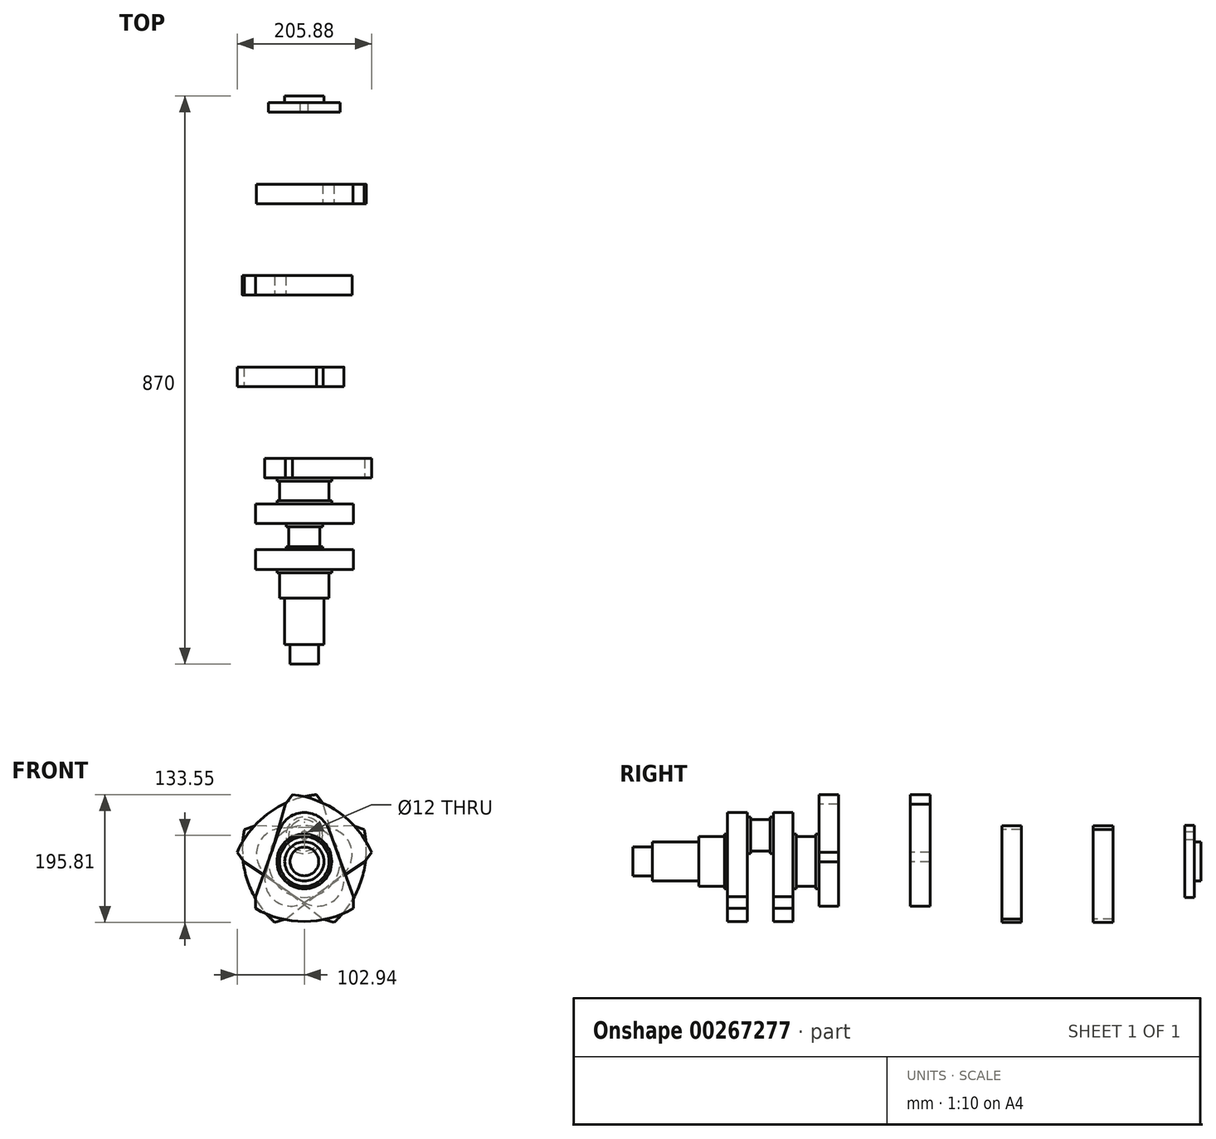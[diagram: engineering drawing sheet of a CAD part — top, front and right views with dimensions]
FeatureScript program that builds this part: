
annotation { "Feature Type Name" : "Feature", "Feature Type Description" : "" }
export const myFeature = defineFeature(function(context is Context, id is Id, definition is map)
    precondition{}
    {
        {
            assignVariable(context, id + "F0", {"name" : "wangen_breite", "anyValue" : 30});
        }
        {
            assignVariable(context, id + "F1", {"name" : "lager_klein_breite", "anyValue" : 40});
        }
        {
            assignVariable(context, id + "F2", {"name" : "lager_gross_breite", "anyValue" : 40});
        }
        {
            assignVariable(context, id + "F3", {"name" : "pleuel_breite", "anyValue" : 2 * getVariable(context, 'wangen_breite') + getVariable(context, 'lager_gross_breite') + getVariable(context, 'lager_klein_breite')});
        }
        {
            var Q0;
            Q0=qCreatedBy(makeId("Front.planeOp"),FACE);
            var sketch = newSketch(context, id + "F4", { "sketchPlane" : qUnion([Q0])});
            skLineSegment(sketch, "E0", {"start": v(-37.59, 48.68) * mm, "end": v(-75, -54.1) * mm});
            skLineSegment(sketch, "E1", {"start": v(-75, -54.1) * mm, "end": v(-75, -71.9) * mm});
            skLineSegment(sketch, "E2", {"start": v(75, -71.9) * mm, "end": v(75, -54.1) * mm});
            skLineSegment(sketch, "E3", {"start": v(75, -54.1) * mm, "end": v(37.59, 48.68) * mm});
            skArc(sketch, "E4", {"start": v(37.59, 48.68) * mm, "mid": v(0, 75) * mm, "end": v(-37.59, 48.68) * mm});
            skArc(sketch, "E5", {"start": v(-75, -71.9) * mm, "mid": v(0, -92) * mm, "end": v(75, -71.9) * mm});
            skSolve(sketch);
        }
        {
            var Q0;
            Q0 = qSketchRegion(id + "F4", true);
            extrude(context, id + "F5", {"entities" : qUnion([Q0]), "oppositeDirection" : true, "depth" : (getVariable(context, 'wangen_breite')) * mm});
        }
        {
            var Q0;
            Q0=qCreatedBy(makeId("Right.planeOp"),FACE);
            var sketch = newSketch(context, id + "F6", { "sketchPlane" : qUnion([Q0])});
            skLineSegment(sketch, "E6", {"start": v(0, 0) * mm, "end": v(0, 28) * mm});
            skLineSegment(sketch, "E7", {"start": v(0, 28) * mm, "end": v(5, 28) * mm});
            skLineSegment(sketch, "E8", {"start": v(5, 28) * mm, "end": v(5, 24) * mm});
            skLineSegment(sketch, "E9", {"start": v(5, 24) * mm, "end": v(35, 24) * mm});
            skLineSegment(sketch, "E10", {"start": v(35, 24) * mm, "end": v(35, 28) * mm});
            skLineSegment(sketch, "E11", {"start": v(35, 28) * mm, "end": v(40, 28) * mm});
            skLineSegment(sketch, "E12", {"start": v(40, 28) * mm, "end": v(40, 0) * mm});
            skLineSegment(sketch, "E13", {"start": v(40, 0) * mm, "end": v(0, 0) * mm});
            skSolve(sketch);
        }
        {
            var Q0;
            Q0 = qSketchRegion(id + "F6", true);
            var Q1;
            Q1=sQuery(id+"F6.wireOp",EDGE,"E13");
            revolve(context, id + "F7", {"entities" : qUnion([Q0]), "axis" : qUnion([Q1]), "revolveType" : RevolveType.FULL});
        }
        {
            var Q0;
            Q0=qCreatedBy(makeId("Right.planeOp"),FACE);
            var sketch = newSketch(context, id + "F8", { "sketchPlane" : qUnion([Q0])});
            skLineSegment(sketch, "E14", {"start": v(0, 0) * mm, "end": v(0, 42) * mm});
            skLineSegment(sketch, "E15", {"start": v(0, 42) * mm, "end": v(5, 42) * mm});
            skLineSegment(sketch, "E16", {"start": v(5, 42) * mm, "end": v(5, 38) * mm});
            skLineSegment(sketch, "E17", {"start": v(5, 38) * mm, "end": v(35, 38) * mm});
            skLineSegment(sketch, "E18", {"start": v(35, 38) * mm, "end": v(35, 42) * mm});
            skLineSegment(sketch, "E19", {"start": v(35, 42) * mm, "end": v(40, 42) * mm});
            skLineSegment(sketch, "E20", {"start": v(40, 42) * mm, "end": v(40, 0) * mm});
            skLineSegment(sketch, "E21", {"start": v(40, 0) * mm, "end": v(0, 0) * mm});
            skSolve(sketch);
        }
        {
            var Q0;
            Q0 = qSketchRegion(id + "F8", true);
            var Q1;
            Q1=sQuery(id+"F8.wireOp",EDGE,"E21");
            revolve(context, id + "F9", {"entities" : qUnion([Q0]), "axis" : qUnion([Q1]), "revolveType" : RevolveType.FULL});
        }
        {
            var Q0;
            Q0=makeQuery(id+"F5.opExtrude","SWEPT_BODY",BODY,{"disambiguationData":[OSD([sQuery(id+"F4.wireOp",EDGE,"E0"),sQuery(id+"F4.wireOp",EDGE,"E1"),sQuery(id+"F4.wireOp",EDGE,"E2"),sQuery(id+"F4.wireOp",EDGE,"E3"),sQuery(id+"F4.wireOp",EDGE,"E4"),sQuery(id+"F4.wireOp",EDGE,"E5")])]});
            var Q1;
            Q1=qCreatedBy(makeId("Front.planeOp"),FACE);
            transform(context, id + "F10", {"entities" : qUnion([Q0]), "transformType" : TransformType.TRANSLATION_DISTANCE, "transformDirection" : qUnion([Q1]), "distance" : (getVariable(context, 'wangen_breite') + getVariable(context, 'lager_klein_breite')) * mm, "oppositeDirection" : true, "makeCopy" : true});
        }
        {
            var Q0;
            Q0=makeQuery(id+"F7.opRevolve","SWEPT_BODY",BODY,{"disambiguationData":[OSD([sQuery(id+"F6.wireOp",EDGE,"E6"),sQuery(id+"F6.wireOp",EDGE,"E7"),sQuery(id+"F6.wireOp",EDGE,"E8"),sQuery(id+"F6.wireOp",EDGE,"E9"),sQuery(id+"F6.wireOp",EDGE,"E10"),sQuery(id+"F6.wireOp",EDGE,"E11"),sQuery(id+"F6.wireOp",EDGE,"E12"),sQuery(id+"F6.wireOp",EDGE,"E13")])]});
            var Q1;
            Q1=qCreatedBy(makeId("Top.planeOp"),FACE);
            transform(context, id + "F11", {"entities" : qUnion([Q0]), "transformType" : TransformType.TRANSLATION_DISTANCE, "transformDirection" : qUnion([Q1]), "distance" : 40 * mm, "makeCopy" : false});
        }
        {
            var Q0;
            Q0=makeQuery(id+"F7.opRevolve","SWEPT_BODY",BODY,{"disambiguationData":[OSD([sQuery(id+"F6.wireOp",EDGE,"E6"),sQuery(id+"F6.wireOp",EDGE,"E7"),sQuery(id+"F6.wireOp",EDGE,"E8"),sQuery(id+"F6.wireOp",EDGE,"E9"),sQuery(id+"F6.wireOp",EDGE,"E10"),sQuery(id+"F6.wireOp",EDGE,"E11"),sQuery(id+"F6.wireOp",EDGE,"E12"),sQuery(id+"F6.wireOp",EDGE,"E13")])]});
            var Q1;
            Q1=qCreatedBy(makeId("Front.planeOp"),FACE);
            transform(context, id + "F12", {"entities" : qUnion([Q0]), "transformType" : TransformType.TRANSLATION_DISTANCE, "transformDirection" : qUnion([Q1]), "distance" : (getVariable(context, 'wangen_breite')) * mm, "oppositeDirection" : true, "makeCopy" : false});
        }
        {
            var Q0;
            Q0=makeQuery(id+"F9.opRevolve","SWEPT_BODY",BODY,{"disambiguationData":[OSD([sQuery(id+"F8.wireOp",EDGE,"E14"),sQuery(id+"F8.wireOp",EDGE,"E15"),sQuery(id+"F8.wireOp",EDGE,"E16"),sQuery(id+"F8.wireOp",EDGE,"E17"),sQuery(id+"F8.wireOp",EDGE,"E18"),sQuery(id+"F8.wireOp",EDGE,"E19"),sQuery(id+"F8.wireOp",EDGE,"E20"),sQuery(id+"F8.wireOp",EDGE,"E21")])]});
            var Q1;
            Q1=qCreatedBy(makeId("Front.planeOp"),FACE);
            transform(context, id + "F13", {"entities" : qUnion([Q0]), "transformType" : TransformType.TRANSLATION_DISTANCE, "transformDirection" : qUnion([Q1]), "distance" : (2 * getVariable(context, 'wangen_breite') + getVariable(context, 'lager_klein_breite')) * mm, "oppositeDirection" : true, "makeCopy" : false});
        }
        {
            var Q0;
            Q0=makeQuery(id+"F5.opExtrude","SWEPT_BODY",BODY,{"disambiguationData":[OSD([sQuery(id+"F4.wireOp",EDGE,"E0"),sQuery(id+"F4.wireOp",EDGE,"E1"),sQuery(id+"F4.wireOp",EDGE,"E2"),sQuery(id+"F4.wireOp",EDGE,"E3"),sQuery(id+"F4.wireOp",EDGE,"E4"),sQuery(id+"F4.wireOp",EDGE,"E5")])]});
            var Q1;
            Q1=qCreatedBy(makeId("Front.planeOp"),FACE);
            transform(context, id + "F14", {"entities" : qUnion([Q0]), "transformType" : TransformType.TRANSLATION_DISTANCE, "transformDirection" : qUnion([Q1]), "distance" : (getVariable(context, 'pleuel_breite')) * mm, "oppositeDirection" : true, "makeCopy" : true});
        }
        {
            var Q0;
            Q0=makeQuery(id+"F5.opExtrude","SWEPT_BODY",BODY,{"disambiguationData":[OSD([sQuery(id+"F4.wireOp",EDGE,"E0"),sQuery(id+"F4.wireOp",EDGE,"E1"),sQuery(id+"F4.wireOp",EDGE,"E2"),sQuery(id+"F4.wireOp",EDGE,"E3"),sQuery(id+"F4.wireOp",EDGE,"E4"),sQuery(id+"F4.wireOp",EDGE,"E5")])]});
            var Q1;
            Q1=qCreatedBy(makeId("Front.planeOp"),FACE);
            transform(context, id + "F15", {"entities" : qUnion([Q0]), "transformType" : TransformType.TRANSLATION_DISTANCE, "transformDirection" : qUnion([Q1]), "distance" : (2 * getVariable(context, 'pleuel_breite')) * mm, "oppositeDirection" : true, "makeCopy" : true});
        }
        {
            var Q0;
            Q0=makeQuery(id+"F5.opExtrude","SWEPT_BODY",BODY,{"disambiguationData":[OSD([sQuery(id+"F4.wireOp",EDGE,"E0"),sQuery(id+"F4.wireOp",EDGE,"E1"),sQuery(id+"F4.wireOp",EDGE,"E2"),sQuery(id+"F4.wireOp",EDGE,"E3"),sQuery(id+"F4.wireOp",EDGE,"E4"),sQuery(id+"F4.wireOp",EDGE,"E5")])]});
            var Q1;
            Q1=qCreatedBy(makeId("Front.planeOp"),FACE);
            transform(context, id + "F16", {"entities" : qUnion([Q0]), "transformType" : TransformType.TRANSLATION_DISTANCE, "transformDirection" : qUnion([Q1]), "distance" : (3 * getVariable(context, 'pleuel_breite')) * mm, "oppositeDirection" : true, "makeCopy" : true});
        }
        {
            var Q0;
            Q0=makeQuery(id+"F5.opExtrude","SWEPT_BODY",BODY,{"disambiguationData":[OSD([sQuery(id+"F4.wireOp",EDGE,"E0"),sQuery(id+"F4.wireOp",EDGE,"E1"),sQuery(id+"F4.wireOp",EDGE,"E2"),sQuery(id+"F4.wireOp",EDGE,"E3"),sQuery(id+"F4.wireOp",EDGE,"E4"),sQuery(id+"F4.wireOp",EDGE,"E5")])]});
            var Q1;
            Q1=qCreatedBy(makeId("Front.planeOp"),FACE);
            transform(context, id + "F17", {"entities" : qUnion([Q0]), "transformType" : TransformType.TRANSLATION_DISTANCE, "transformDirection" : qUnion([Q1]), "distance" : (4 * getVariable(context, 'pleuel_breite')) * mm, "oppositeDirection" : true, "makeCopy" : true});
        }
        {
            var Q0;
            Q0=makeQuery(id+"F17.opPattern","COPY",BODY,{"derivedFrom":makeQuery(id+"F5.opExtrude","SWEPT_BODY",BODY,{"disambiguationData":[OSD([sQuery(id+"F4.wireOp",EDGE,"E0"),sQuery(id+"F4.wireOp",EDGE,"E1"),sQuery(id+"F4.wireOp",EDGE,"E2"),sQuery(id+"F4.wireOp",EDGE,"E3"),sQuery(id+"F4.wireOp",EDGE,"E4"),sQuery(id+"F4.wireOp",EDGE,"E5")])]}),"instanceName":"1"});
            var Q1;
            Q1=makeQuery(id+"F9.opRevolve","SWEPT_FACE",FACE,{"disambiguationData":[OSD([sQuery(id+"F8.wireOp",EDGE,"E17")])]});
            transform(context, id + "F18", {"entities" : qUnion([Q0]), "transformType" : TransformType.ROTATION, "transformAxis" : qUnion([Q1]), "angle" : 72 * degree, "oppositeDirection" : true, "makeCopy" : false});
        }
        {
            var Q0;
            Q0=makeQuery(id+"F16.opPattern","COPY",BODY,{"derivedFrom":makeQuery(id+"F5.opExtrude","SWEPT_BODY",BODY,{"disambiguationData":[OSD([sQuery(id+"F4.wireOp",EDGE,"E0"),sQuery(id+"F4.wireOp",EDGE,"E1"),sQuery(id+"F4.wireOp",EDGE,"E2"),sQuery(id+"F4.wireOp",EDGE,"E3"),sQuery(id+"F4.wireOp",EDGE,"E4"),sQuery(id+"F4.wireOp",EDGE,"E5")])]}),"instanceName":"1"});
            var Q1;
            Q1=makeQuery(id+"F9.opRevolve","SWEPT_FACE",FACE,{"disambiguationData":[OSD([sQuery(id+"F8.wireOp",EDGE,"E17")])]});
            transform(context, id + "F19", {"entities" : qUnion([Q0]), "transformType" : TransformType.ROTATION, "transformAxis" : qUnion([Q1]), "angle" : 288 * degree, "oppositeDirection" : true, "makeCopy" : false});
        }
        {
            var Q0;
            Q0=makeQuery(id+"F15.opPattern","COPY",BODY,{"derivedFrom":makeQuery(id+"F5.opExtrude","SWEPT_BODY",BODY,{"disambiguationData":[OSD([sQuery(id+"F4.wireOp",EDGE,"E0"),sQuery(id+"F4.wireOp",EDGE,"E1"),sQuery(id+"F4.wireOp",EDGE,"E2"),sQuery(id+"F4.wireOp",EDGE,"E3"),sQuery(id+"F4.wireOp",EDGE,"E4"),sQuery(id+"F4.wireOp",EDGE,"E5")])]}),"instanceName":"1"});
            var Q1;
            Q1=makeQuery(id+"F9.opRevolve","SWEPT_FACE",FACE,{"disambiguationData":[OSD([sQuery(id+"F8.wireOp",EDGE,"E17")])]});
            transform(context, id + "F20", {"entities" : qUnion([Q0]), "transformType" : TransformType.ROTATION, "transformAxis" : qUnion([Q1]), "angle" : 216 * degree, "oppositeDirection" : true, "makeCopy" : false});
        }
        {
            var Q0;
            Q0=makeQuery(id+"F14.opPattern","COPY",BODY,{"derivedFrom":makeQuery(id+"F5.opExtrude","SWEPT_BODY",BODY,{"disambiguationData":[OSD([sQuery(id+"F4.wireOp",EDGE,"E0"),sQuery(id+"F4.wireOp",EDGE,"E1"),sQuery(id+"F4.wireOp",EDGE,"E2"),sQuery(id+"F4.wireOp",EDGE,"E3"),sQuery(id+"F4.wireOp",EDGE,"E4"),sQuery(id+"F4.wireOp",EDGE,"E5")])]}),"instanceName":"1"});
            var Q1;
            Q1=makeQuery(id+"F9.opRevolve","SWEPT_FACE",FACE,{"disambiguationData":[OSD([sQuery(id+"F8.wireOp",EDGE,"E17")])]});
            transform(context, id + "F21", {"entities" : qUnion([Q0]), "transformType" : TransformType.ROTATION, "transformAxis" : qUnion([Q1]), "angle" : 144 * degree, "oppositeDirection" : true, "makeCopy" : false});
        }
        {
            var Q0;
            Q0=qCreatedBy(makeId("Right.planeOp"),FACE);
            var sketch = newSketch(context, id + "F22", { "sketchPlane" : qUnion([Q0])});
            skLineSegment(sketch, "E22", {"start": v(0, 0) * mm, "end": v(-145, 0) * mm});
            skLineSegment(sketch, "E23", {"start": v(-145, 0) * mm, "end": v(-145, 22) * mm});
            skLineSegment(sketch, "E24", {"start": v(-145, 22) * mm, "end": v(-115, 22) * mm});
            skLineSegment(sketch, "E25", {"start": v(-115, 22) * mm, "end": v(-115, 30) * mm});
            skLineSegment(sketch, "E26", {"start": v(-115, 30) * mm, "end": v(-44, 30) * mm});
            skLineSegment(sketch, "E27", {"start": v(-44, 30) * mm, "end": v(-44, 38) * mm});
            skLineSegment(sketch, "E28", {"start": v(-44, 38) * mm, "end": v(-5, 38) * mm});
            skLineSegment(sketch, "E29", {"start": v(-5, 38) * mm, "end": v(-5, 42) * mm});
            skLineSegment(sketch, "E30", {"start": v(-5, 42) * mm, "end": v(0, 42) * mm});
            skLineSegment(sketch, "E31", {"start": v(0, 42) * mm, "end": v(0, 0) * mm});
            skSolve(sketch);
        }
        {
            var Q0;
            Q0 = qSketchRegion(id + "F22", true);
            var Q1;
            Q1=sQuery(id+"F22.wireOp",EDGE,"E22");
            revolve(context, id + "F23", {"entities" : qUnion([Q0]), "axis" : qUnion([Q1]), "revolveType" : RevolveType.FULL});
        }
        {
            var Q0;
            Q0=qCreatedBy(makeId("Right.planeOp"),FACE);
            var sketch = newSketch(context, id + "F24", { "sketchPlane" : qUnion([Q0])});
            skLineSegment(sketch, "E32", {"start": v(0, 0) * mm, "end": v(0, 55) * mm});
            skLineSegment(sketch, "E33", {"start": v(0, 55) * mm, "end": v(15, 55) * mm});
            skLineSegment(sketch, "E34", {"start": v(15, 55) * mm, "end": v(15, 30) * mm});
            skLineSegment(sketch, "E35", {"start": v(15, 30) * mm, "end": v(25, 30) * mm});
            skLineSegment(sketch, "E36", {"start": v(25, 30) * mm, "end": v(25, 0) * mm});
            skLineSegment(sketch, "E37", {"start": v(25, 0) * mm, "end": v(0, 0) * mm});
            skSolve(sketch);
        }
        {
            var Q0;
            Q0 = qSketchRegion(id + "F24", true);
            var Q1;
            Q1=sQuery(id+"F24.wireOp",EDGE,"E37");
            revolve(context, id + "F25", {"entities" : qUnion([Q0]), "axis" : qUnion([Q1]), "revolveType" : RevolveType.FULL});
        }
        {
            var Q0;
            Q0=makeQuery(id+"F25.opRevolve","SWEPT_FACE",FACE,{"disambiguationData":[OSD([sQuery(id+"F24.wireOp",EDGE,"E34")])]});
            var sketch = newSketch(context, id + "F26", { "sketchPlane" : qUnion([Q0])});
            skPoint(sketch, "E38", {"position": v(0, 40) * mm});
            skSolve(sketch);
        }
        {
            var Q0;
            Q0=sQuery(id+"F26.wireOp",VERTEX,"E38");
            var Q1;
            Q1=makeQuery(id+"F25.opRevolve","SWEPT_BODY",BODY,{"disambiguationData":[OSD([sQuery(id+"F24.wireOp",EDGE,"E32"),sQuery(id+"F24.wireOp",EDGE,"E33"),sQuery(id+"F24.wireOp",EDGE,"E34"),sQuery(id+"F24.wireOp",EDGE,"E35"),sQuery(id+"F24.wireOp",EDGE,"E36"),sQuery(id+"F24.wireOp",EDGE,"E37")])]});
            hole(context, id + "F27", {"style" : HoleStyle.SIMPLE, "endStyle" : HoleEndStyle.THROUGH, "holeDiameter" : 12 * mm, "tappedDepth" : 12 * mm, "tapClearance" : 3, "locations" : qUnion([Q0]), "scope" : qUnion([Q1])});
        }
        {
            var Q0;
            Q0=makeQuery(id+"F25.opRevolve","SWEPT_BODY",BODY,{"disambiguationData":[OSD([sQuery(id+"F24.wireOp",EDGE,"E32"),sQuery(id+"F24.wireOp",EDGE,"E33"),sQuery(id+"F24.wireOp",EDGE,"E34"),sQuery(id+"F24.wireOp",EDGE,"E35"),sQuery(id+"F24.wireOp",EDGE,"E36"),sQuery(id+"F24.wireOp",EDGE,"E37")])]});
            var Q1;
            Q1=qCreatedBy(makeId("Front.planeOp"),FACE);
            transform(context, id + "F28", {"entities" : qUnion([Q0]), "transformType" : TransformType.TRANSLATION_DISTANCE, "transformDirection" : qUnion([Q1]), "distance" : (5 * getVariable(context, 'pleuel_breite')) * mm, "oppositeDirection" : true, "makeCopy" : false});
        }
    });
